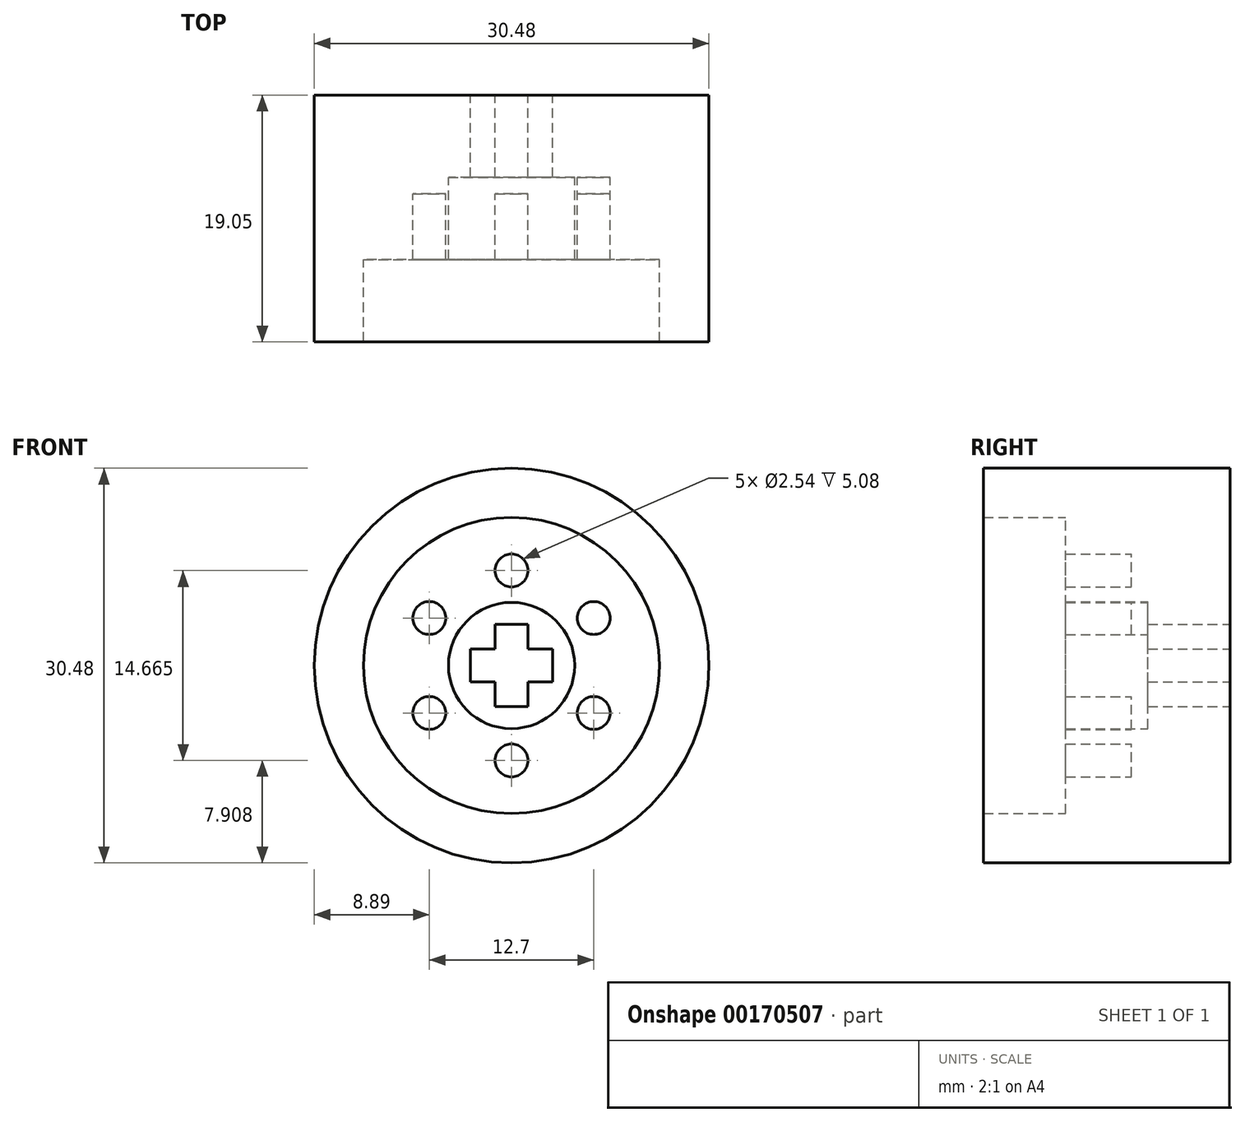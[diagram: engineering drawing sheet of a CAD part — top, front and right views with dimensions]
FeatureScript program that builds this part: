
annotation { "Feature Type Name" : "Feature", "Feature Type Description" : "" }
export const myFeature = defineFeature(function(context is Context, id is Id, definition is map)
    precondition{}
    {
        {
            var Q0;
            Q0=qCreatedBy(makeId("Front.planeOp"),FACE);
            var sketch = newSketch(context, id + "F0", { "sketchPlane" : qUnion([Q0])});
            skCircle(sketch, "E0", {"center": v(0, 0) * mm, "radius": 12.7 * mm});
            skCircle(sketch, "E1", {"center": v(0, 0) * mm, "radius": 15.24 * mm});
            skLineSegment(sketch, "E2.bottom", {"start": v(3.17, -1.27) * mm, "end": v(-3.18, -1.27) * mm});
            skLineSegment(sketch, "E2.top", {"start": v(3.17, 1.27) * mm, "end": v(-3.18, 1.27) * mm});
            skLineSegment(sketch, "E2.left", {"start": v(3.17, -1.27) * mm, "end": v(3.17, 1.27) * mm});
            skLineSegment(sketch, "E2.right", {"start": v(-3.18, -1.27) * mm, "end": v(-3.18, 1.27) * mm});
            skLineSegment(sketch, "E3.bottom", {"start": v(1.27, -3.18) * mm, "end": v(-1.27, -3.18) * mm});
            skLineSegment(sketch, "E3.top", {"start": v(1.27, 3.17) * mm, "end": v(-1.27, 3.17) * mm});
            skLineSegment(sketch, "E3.left", {"start": v(1.27, -3.18) * mm, "end": v(1.27, 3.17) * mm});
            skLineSegment(sketch, "E3.right", {"start": v(-1.27, -3.18) * mm, "end": v(-1.27, 3.17) * mm});
            skCircle(sketch, "E4", {"center": v(0, 0) * mm, "radius": 11.43 * mm});
            skPoint(sketch, "E5.cCircle.perimeterSnap0", {"position": v(3.17, 0) * mm});
            skPoint(sketch, "E5.0.midPoint", {"position": v(3.17, -5.5) * mm});
            skPoint(sketch, "E5.0.midPoint.positionSnap0", {"position": v(3.17, 0) * mm});
            skCircle(sketch, "E6", {"center": v(0, 7.33) * mm, "radius": 1.27 * mm});
            skCircle(sketch, "E7", {"center": v(6.35, 3.67) * mm, "radius": 1.27 * mm});
            skCircle(sketch, "E8", {"center": v(6.35, -3.67) * mm, "radius": 1.27 * mm});
            skCircle(sketch, "E9", {"center": v(0, -7.33) * mm, "radius": 1.27 * mm});
            skCircle(sketch, "E10", {"center": v(-6.35, -3.67) * mm, "radius": 1.27 * mm});
            skCircle(sketch, "E11", {"center": v(-6.35, 3.67) * mm, "radius": 1.27 * mm});
            skCircle(sketch, "E12", {"center": v(0, 0) * mm, "radius": 4.87 * mm});
            skSolve(sketch);
        }
        {
            var Q0;
            Q0=makeQuery(id+"F0.imprint","IMPRINT",FACE,{"disambiguationData":[TD([[makeQuery(id+"F0.imprint","IMPRINT",EDGE,{"derivedFrom":sQuery(id+"F0.wireOp",EDGE,"E0")}),-1.0]])]});
            var Q1;
            Q1=makeQuery(id+"F0.imprint","IMPRINT",FACE,{"disambiguationData":[TD([[makeQuery(id+"F0.imprint","IMPRINT",EDGE,{"derivedFrom":sQuery(id+"F0.wireOp",EDGE,"E0")}),1.0]])]});
            extrude(context, id + "F1", {"entities" : qUnion([Q0, Q1]), "depth" : 19.05 * mm});
        }
        {
            var Q0;
            Q0=makeQuery(id+"F0.imprint","IMPRINT",FACE,{"disambiguationData":[TD([[makeQuery(id+"F0.imprint","IMPRINT",EDGE,{"derivedFrom":sQuery(id+"F0.wireOp",EDGE,"E4")}),1.0]])]});
            extrude(context, id + "F2", {"entities" : qUnion([Q0]), "operationType" : NewBodyOperationType.ADD, "depth" : 12.7 * mm});
        }
        {
            var Q0;
            {var subQ5=sQuery(id+"F0.wireOp",EDGE,"E2.left");Q0=makeQuery(id+"F0.imprint","IMPRINT",FACE,{"disambiguationData":[TD([[makeQuery(id+"F0.imprint","IMPRINT",EDGE,{"derivedFrom":subQ5}),-1.0]])]});}
            var Q1;
            Q1=makeQuery(id+"F0.imprint","IMPRINT",FACE,{"disambiguationData":[TD([[makeQuery(id+"F0.imprint","IMPRINT",EDGE,{"derivedFrom":sQuery(id+"F0.wireOp",EDGE,"E7")}),1.0]])]});
            extrude(context, id + "F3", {"entities" : qUnion([Q0, Q1]), "operationType" : NewBodyOperationType.ADD, "depth" : 6.35 * mm});
        }
        {
            var Q0;
            {var subQ0=sQuery(id+"F0.wireOp",EDGE,"E12");var subQ1=sQuery(id+"F0.wireOp",EDGE,"E4");Q0=makeQuery(id+"F3.boolean.opBoolean","MERGE",FACE,{"derivedFrom":[makeQuery(id+"F2.boolean.opBoolean","MERGE",FACE,{"derivedFrom":[makeQuery(id+"F1.opExtrude","CAP_FACE",FACE,{"disambiguationData":[OSD([sQuery(id+"F0.wireOp",EDGE,"E1"),subQ1])],"isStart":true}),makeQuery(id+"F2.opExtrude","CAP_FACE",FACE,{"disambiguationData":[OSD([subQ1,sQuery(id+"F0.wireOp",EDGE,"E6"),sQuery(id+"F0.wireOp",EDGE,"E7"),sQuery(id+"F0.wireOp",EDGE,"E8"),sQuery(id+"F0.wireOp",EDGE,"E9"),sQuery(id+"F0.wireOp",EDGE,"E10"),sQuery(id+"F0.wireOp",EDGE,"E11"),subQ0])],"isStart":true})]}),makeQuery(id+"F3.opExtrude","CAP_FACE",FACE,{"disambiguationData":[OSD([sQuery(id+"F0.wireOp",EDGE,"E2.bottom"),sQuery(id+"F0.wireOp",EDGE,"E2.top"),sQuery(id+"F0.wireOp",EDGE,"E2.left"),sQuery(id+"F0.wireOp",EDGE,"E2.right"),sQuery(id+"F0.wireOp",EDGE,"E3.bottom"),sQuery(id+"F0.wireOp",EDGE,"E3.top"),sQuery(id+"F0.wireOp",EDGE,"E3.left"),sQuery(id+"F0.wireOp",EDGE,"E3.right"),subQ0])],"isStart":true})]});}
            var sketch = newSketch(context, id + "F4", { "sketchPlane" : qUnion([Q0])});
            skCircle(sketch, "E13", {"center": v(0, 0) * mm, "radius": 4.7 * mm});
            skCircle(sketch, "E14", {"center": v(0, 0) * mm, "radius": 15.24 * mm});
            skLineSegment(sketch, "E15", {"start": v(-1.27, 7.33) * mm, "end": v(-1.27, 15.19) * mm});
            skLineSegment(sketch, "E16", {"start": v(-1.27, 15.19) * mm, "end": v(-1.27, 4.53) * mm});
            skLineSegment(sketch, "E17", {"start": v(1.27, 4.53) * mm, "end": v(1.27, 15.19) * mm});
            skLineSegment(sketch, "E18.1.0", {"start": v(-13.14, 6.38) * mm, "end": v(-3.9, 1.05) * mm});
            skLineSegment(sketch, "E18.1.1", {"start": v(-2.64, 3.25) * mm, "end": v(-11.87, 8.58) * mm});
            skLineSegment(sketch, "E18.2.0", {"start": v(-11.45, -8.3) * mm, "end": v(-2.22, -2.97) * mm});
            skLineSegment(sketch, "E18.2.1", {"start": v(-3.49, -0.77) * mm, "end": v(-12.72, -6.1) * mm});
            skLineSegment(sketch, "E18.3.0", {"start": v(2.1, -14.18) * mm, "end": v(2.1, -3.52) * mm});
            skLineSegment(sketch, "E18.3.1", {"start": v(-0.43, -3.52) * mm, "end": v(-0.43, -14.18) * mm});
            skLineSegment(sketch, "E18.4.0", {"start": v(13.98, -5.37) * mm, "end": v(4.75, -0.04) * mm});
            skLineSegment(sketch, "E18.4.1", {"start": v(3.48, -2.24) * mm, "end": v(12.71, -7.57) * mm});
            skLineSegment(sketch, "E18.5.0", {"start": v(12.3, 9.3) * mm, "end": v(3.06, 3.98) * mm});
            skLineSegment(sketch, "E18.5.1", {"start": v(4.33, 1.78) * mm, "end": v(13.56, 7.1) * mm});
            skPoint(sketch, "E18.center", {"position": v(0.42, 0.5) * mm});
            skCircle(sketch, "E19", {"center": v(0, 0) * mm, "radius": 12.7 * mm});
            skSolve(sketch);
        }
        {
            var Q0;
            Q0=makeQuery(id+"F0.imprint","IMPRINT",FACE,{"disambiguationData":[TD([[makeQuery(id+"F0.imprint","IMPRINT",EDGE,{"derivedFrom":sQuery(id+"F0.wireOp",EDGE,"E9")}),1.0]])]});
            var Q1;
            Q1 = qSketchRegion(id + "F4", true);
            extrude(context, id + "F5", {"entities" : qUnion([Q0, Q1]), "operationType" : NewBodyOperationType.ADD, "depth" : 7.62 * mm});
        }
        {
            var Q0;
            Q0 = qSketchRegion(id + "F0", true);
            var Q1;
            {var subQ0=sQuery(id+"F4.wireOp",EDGE,"E18.2.1");var subQ1=makeQuery(id+"F2.opExtrude","CAP_EDGE",EDGE,{"disambiguationData":[OSD([sQuery(id+"F0.wireOp",EDGE,"E8")])],"isStart":true});var subQ2=makeQuery(id+"F4.imprint","INTERSECT",VERTEX,{"disambiguationData":[OD(0.0)],"derivedFrom":[subQ1,subQ0]});Q1=makeQuery(id+"F4.imprint","IMPRINT",FACE,{"disambiguationData":[TD([[makeQuery(id+"F4.imprint","IMPRINT",EDGE,{"disambiguationData":[TD([[subQ2,-1.0]])],"derivedFrom":subQ0}),1.0]])]});}
            var Q2;
            {var subQ0=makeQuery(id+"F2.opExtrude","CAP_EDGE",EDGE,{"disambiguationData":[OSD([sQuery(id+"F0.wireOp",EDGE,"E6")])],"isStart":true});var subQ1=makeQuery(id+"F4.imprint","INTERSECT",VERTEX,{"derivedFrom":[subQ0,sQuery(id+"F4.wireOp",EDGE,"E16")]});Q2=makeQuery(id+"F4.imprint","IMPRINT",FACE,{"disambiguationData":[TD([[makeQuery(id+"F4.imprint","IMPRINT",EDGE,{"disambiguationData":[TD([[subQ1,1.0]])],"derivedFrom":subQ0}),-1.0]])]});}
            var Q3;
            {var subQ0=sQuery(id+"F4.wireOp",EDGE,"E18.5.1");var subQ1=makeQuery(id+"F2.opExtrude","CAP_EDGE",EDGE,{"disambiguationData":[OSD([sQuery(id+"F0.wireOp",EDGE,"E11")])],"isStart":true});var subQ2=makeQuery(id+"F4.imprint","INTERSECT",VERTEX,{"disambiguationData":[OD(0.0)],"derivedFrom":[subQ1,subQ0]});Q3=makeQuery(id+"F4.imprint","IMPRINT",FACE,{"disambiguationData":[TD([[makeQuery(id+"F4.imprint","IMPRINT",EDGE,{"disambiguationData":[TD([[subQ2,-1.0]])],"derivedFrom":subQ0}),1.0]])]});}
            var Q4;
            {var subQ0=sQuery(id+"F4.wireOp",EDGE,"E18.4.1");var subQ1=makeQuery(id+"F2.opExtrude","CAP_EDGE",EDGE,{"disambiguationData":[OSD([sQuery(id+"F0.wireOp",EDGE,"E10")])],"isStart":true});var subQ2=makeQuery(id+"F4.imprint","INTERSECT",VERTEX,{"disambiguationData":[OD(0.0)],"derivedFrom":[subQ1,subQ0]});Q4=makeQuery(id+"F4.imprint","IMPRINT",FACE,{"disambiguationData":[TD([[makeQuery(id+"F4.imprint","IMPRINT",EDGE,{"disambiguationData":[TD([[subQ2,-1.0]])],"derivedFrom":subQ0}),1.0]])]});}
            var Q5;
            {var subQ0=sQuery(id+"F4.wireOp",EDGE,"E18.4.1");var subQ1=makeQuery(id+"F2.opExtrude","CAP_EDGE",EDGE,{"disambiguationData":[OSD([sQuery(id+"F0.wireOp",EDGE,"E10")])],"isStart":true});var subQ2=makeQuery(id+"F4.imprint","INTERSECT",VERTEX,{"disambiguationData":[OD(0.0)],"derivedFrom":[subQ1,subQ0]});Q5=makeQuery(id+"F4.imprint","IMPRINT",FACE,{"disambiguationData":[TD([[makeQuery(id+"F4.imprint","IMPRINT",EDGE,{"disambiguationData":[TD([[subQ2,-1.0]])],"derivedFrom":subQ0}),-1.0]])]});}
            var Q6;
            {var subQ0=sQuery(id+"F4.wireOp",EDGE,"E18.5.1");var subQ1=makeQuery(id+"F2.opExtrude","CAP_EDGE",EDGE,{"disambiguationData":[OSD([sQuery(id+"F0.wireOp",EDGE,"E11")])],"isStart":true});var subQ2=makeQuery(id+"F4.imprint","INTERSECT",VERTEX,{"disambiguationData":[OD(0.0)],"derivedFrom":[subQ1,subQ0]});Q6=makeQuery(id+"F4.imprint","IMPRINT",FACE,{"disambiguationData":[TD([[makeQuery(id+"F4.imprint","IMPRINT",EDGE,{"disambiguationData":[TD([[subQ2,-1.0]])],"derivedFrom":subQ0}),-1.0]])]});}
            var Q7;
            Q7=makeQuery(id+"F0.imprint","IMPRINT",FACE,{"disambiguationData":[TD([[makeQuery(id+"F0.imprint","IMPRINT",EDGE,{"derivedFrom":sQuery(id+"F0.wireOp",EDGE,"E8")}),1.0]])]});
            extrude(context, id + "F6", {"entities" : qUnion([Q0, Q1, Q2, Q3, Q4, Q5, Q6, Q7]), "operationType" : NewBodyOperationType.ADD, "depth" : 7.62 * mm});
        }
        {
            var Q0;
            {var subQ0=sQuery(id+"F0.wireOp",EDGE,"E11");var subQ1=sQuery(id+"F0.wireOp",EDGE,"E10");var subQ2=sQuery(id+"F0.wireOp",EDGE,"E6");var subQ3=sQuery(id+"F0.wireOp",EDGE,"E8");var subQ4=sQuery(id+"F0.wireOp",EDGE,"E9");var subQ5=sQuery(id+"F0.wireOp",EDGE,"E7");var subQ6=sQuery(id+"F0.wireOp",EDGE,"E12");var subQ7=sQuery(id+"F0.wireOp",EDGE,"E4");Q0=makeQuery(id+"F6.boolean.opBoolean","MERGE",FACE,{"derivedFrom":[makeQuery(id+"F5.boolean.opBoolean","MERGE",FACE,{"derivedFrom":[makeQuery(id+"F3.boolean.opBoolean","MERGE",FACE,{"derivedFrom":[makeQuery(id+"F2.boolean.opBoolean","MERGE",FACE,{"derivedFrom":[makeQuery(id+"F1.opExtrude","CAP_FACE",FACE,{"disambiguationData":[OSD([sQuery(id+"F0.wireOp",EDGE,"E1"),subQ7])],"isStart":true}),makeQuery(id+"F2.opExtrude","CAP_FACE",FACE,{"disambiguationData":[OSD([subQ7,subQ2,subQ5,subQ3,subQ4,subQ1,subQ0,subQ6])],"isStart":true})]}),makeQuery(id+"F3.opExtrude","CAP_FACE",FACE,{"disambiguationData":[OSD([sQuery(id+"F0.wireOp",EDGE,"E2.bottom"),sQuery(id+"F0.wireOp",EDGE,"E2.top"),sQuery(id+"F0.wireOp",EDGE,"E2.left"),sQuery(id+"F0.wireOp",EDGE,"E2.right"),sQuery(id+"F0.wireOp",EDGE,"E3.bottom"),sQuery(id+"F0.wireOp",EDGE,"E3.top"),sQuery(id+"F0.wireOp",EDGE,"E3.left"),sQuery(id+"F0.wireOp",EDGE,"E3.right"),subQ6])],"isStart":true}),makeQuery(id+"F3.opExtrude","CAP_FACE",FACE,{"disambiguationData":[OSD([subQ5])],"isStart":true})]}),makeQuery(id+"F5.opExtrude","CAP_FACE",FACE,{"disambiguationData":[OSD([subQ4])],"isStart":true})]}),makeQuery(id+"F6.opExtrude","CAP_FACE",FACE,{"disambiguationData":[OSD([subQ3])],"isStart":true}),makeQuery(id+"F6.opExtrude","CAP_FACE",FACE,{"disambiguationData":[OSD([subQ2])],"isStart":true}),makeQuery(id+"F6.opExtrude","CAP_FACE",FACE,{"disambiguationData":[OSD([subQ1])],"isStart":true}),makeQuery(id+"F6.opExtrude","CAP_FACE",FACE,{"disambiguationData":[OSD([subQ0])],"isStart":true})]});}
            var sketch = newSketch(context, id + "F7", { "sketchPlane" : qUnion([Q0])});
            skPoint(sketch, "E20.0.midPoint", {"position": v(5.85, 3.37) * mm});
            skPoint(sketch, "E21.endSnap0", {"position": v(1.27, 2.22) * mm});
            skCircle(sketch, "E22", {"center": v(0, 0) * mm, "radius": 13.34 * mm});
            skCircle(sketch, "E23", {"center": v(0, 0) * mm, "radius": 3.18 * mm});
            skLineSegment(sketch, "E24", {"start": v(2.33, 8.3) * mm, "end": v(0, 3.17) * mm});
            skLineSegment(sketch, "E25", {"start": v(0, 3.17) * mm, "end": v(4.27, 12.63) * mm});
            skLineSegment(sketch, "E26", {"start": v(4.51, 7) * mm, "end": v(1.99, 2.48) * mm});
            skLineSegment(sketch, "E27", {"start": v(1.99, 2.48) * mm, "end": v(6.96, 11.38) * mm});
            skLineSegment(sketch, "E28.1.0", {"start": v(-1.74, 2.65) * mm, "end": v(-8.67, 10.13) * mm});
            skLineSegment(sketch, "E28.1.1", {"start": v(-3.02, 0.98) * mm, "end": v(-10.7, 7.97) * mm});
            skLineSegment(sketch, "E28.2.0", {"start": v(-3.06, -0.84) * mm, "end": v(-12.32, -5.11) * mm});
            skLineSegment(sketch, "E28.2.1", {"start": v(-1.87, -2.57) * mm, "end": v(-10.88, -7.7) * mm});
            skLineSegment(sketch, "E28.3.0", {"start": v(-0.15, -3.17) * mm, "end": v(1.06, -13.3) * mm});
            skLineSegment(sketch, "E28.3.1", {"start": v(1.87, -2.57) * mm, "end": v(3.97, -12.73) * mm});
            skLineSegment(sketch, "E28.4.0", {"start": v(2.97, -1.12) * mm, "end": v(12.97, -3.1) * mm});
            skLineSegment(sketch, "E28.4.1", {"start": v(3.02, 0.98) * mm, "end": v(13.33, -0.16) * mm});
            skSolve(sketch);
        }
        {
            var Q0;
            Q0=sQuery(id+"F7.wireOp",EDGE,"E28.1.0");
            var Q1;
            Q1=sQuery(id+"F7.wireOp",EDGE,"E28.1.1");
            var Q2;
            Q2=sQuery(id+"F7.wireOp",EDGE,"E28.2.0");
            var Q3;
            Q3=sQuery(id+"F7.wireOp",EDGE,"E28.2.1");
            var Q4;
            Q4=sQuery(id+"F7.wireOp",EDGE,"E28.3.0");
            var Q5;
            Q5=sQuery(id+"F7.wireOp",EDGE,"E28.3.1");
            var Q6;
            Q6=sQuery(id+"F7.wireOp",EDGE,"E28.4.0");
            var Q7;
            Q7=sQuery(id+"F7.wireOp",EDGE,"E28.4.1");
            var Q8;
            Q8=sQuery(id+"F7.wireOp",EDGE,"E27");
            extrude(context, id + "F8", {"bodyType" : ToolBodyType.SURFACE, "surfaceEntities" : qUnion([Q0, Q1, Q2, Q3, Q4, Q5, Q6, Q7, Q8]), "depth" : 0.25 * mm});
        }
        {
            var Q0;
            Q0=sQuery(id+"F7.wireOp",EDGE,"E25");
            extrude(context, id + "F9", {"bodyType" : ToolBodyType.SURFACE, "surfaceEntities" : qUnion([Q0]), "depth" : 0.25 * mm});
        }
    });
